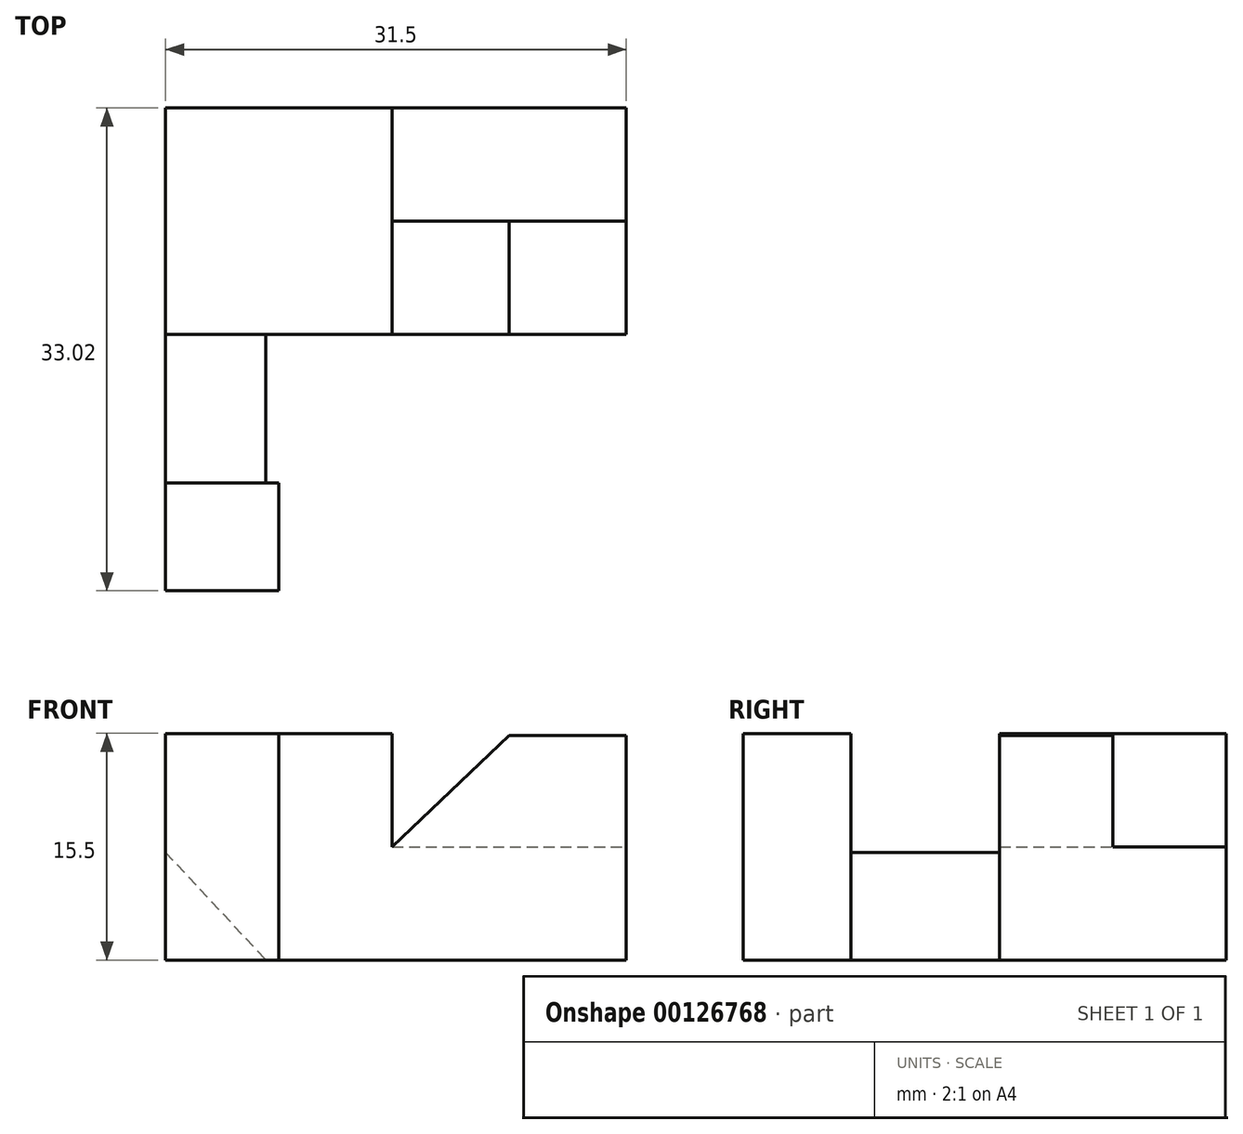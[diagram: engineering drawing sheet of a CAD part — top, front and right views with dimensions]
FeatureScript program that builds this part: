
annotation { "Feature Type Name" : "Feature", "Feature Type Description" : "" }
export const myFeature = defineFeature(function(context is Context, id is Id, definition is map)
    precondition{}
    {
        {
            var Q0;
            Q0=qCreatedBy(makeId("Front.planeOp"),FACE);
            var sketch = newSketch(context, id + "F0", { "sketchPlane" : qUnion([Q0])});
            skLineSegment(sketch, "E0.bottom", {"start": v(7.75, 7.75) * mm, "end": v(-7.75, 7.75) * mm});
            skLineSegment(sketch, "E0.top", {"start": v(7.75, -7.75) * mm, "end": v(-7.75, -7.75) * mm});
            skLineSegment(sketch, "E0.left", {"start": v(7.75, 7.75) * mm, "end": v(7.75, -7.75) * mm});
            skLineSegment(sketch, "E0.right", {"start": v(-7.75, 7.75) * mm, "end": v(-7.75, -7.75) * mm});
            skPoint(sketch, "E0.middle", {"position": v(0, 0) * mm});
            skSolve(sketch);
        }
        {
            var Q0;
            Q0=makeQuery(id+"F0.imprint","IMPRINT",FACE,{"disambiguationData":[TD([[makeQuery(id+"F0.imprint","IMPRINT",EDGE,{"derivedFrom":sQuery(id+"F0.wireOp",EDGE,"E0.bottom")}),1.0]])]});
            extrude(context, id + "F1", {"entities" : qUnion([Q0]), "endBound" : BoundingType.SYMMETRIC, "depth" : 15.5 * mm});
        }
        {
            var Q0;
            Q0=makeQuery(id+"F1.opExtrude","CAP_FACE",FACE,{"disambiguationData":[OSD([sQuery(id+"F0.wireOp",EDGE,"E0.bottom"),sQuery(id+"F0.wireOp",EDGE,"E0.top"),sQuery(id+"F0.wireOp",EDGE,"E0.left"),sQuery(id+"F0.wireOp",EDGE,"E0.right")])],"isStart":false});
            var sketch = newSketch(context, id + "F2", { "sketchPlane" : qUnion([Q0])});
            skLineSegment(sketch, "E1", {"start": v(-7.75, -7.75) * mm, "end": v(-7.75, -0.38) * mm});
            skLineSegment(sketch, "E2", {"start": v(-7.75, -7.75) * mm, "end": v(-0.89, -7.75) * mm});
            skLineSegment(sketch, "E3", {"start": v(-7.75, -0.38) * mm, "end": v(-0.89, -7.75) * mm});
            skSolve(sketch);
        }
        {
            var Q0;
            Q0=makeQuery(id+"F2.imprint","IMPRINT",FACE,{"disambiguationData":[TD([[makeQuery(id+"F2.imprint","IMPRINT",EDGE,{"derivedFrom":sQuery(id+"F2.wireOp",EDGE,"E1")}),1.0]])]});
            extrude(context, id + "F3", {"entities" : qUnion([Q0]), "operationType" : NewBodyOperationType.ADD, "depth" : 10.16 * mm});
        }
        {
            var Q0;
            Q0=makeQuery(id+"F3.opExtrude","CAP_FACE",FACE,{"disambiguationData":[OSD([sQuery(id+"F2.wireOp",EDGE,"E1"),sQuery(id+"F2.wireOp",EDGE,"E2"),sQuery(id+"F2.wireOp",EDGE,"E3")])],"isStart":false});
            var sketch = newSketch(context, id + "F4", { "sketchPlane" : qUnion([Q0])});
            skLineSegment(sketch, "E4.0", {"start": v(7.75, 7.75) * mm, "end": v(-7.75, 7.75) * mm});
            skLineSegment(sketch, "E5.0", {"start": v(7.75, -7.75) * mm, "end": v(-0.89, -7.75) * mm});
            skLineSegment(sketch, "E6", {"start": v(-7.75, 7.75) * mm, "end": v(-7.75, -7.75) * mm});
            skLineSegment(sketch, "E7", {"start": v(-7.75, -7.75) * mm, "end": v(0, -7.75) * mm});
            skLineSegment(sketch, "E8", {"start": v(0, -7.75) * mm, "end": v(0, 7.75) * mm});
            skSolve(sketch);
        }
        {
            var Q0;
            Q0 = qSketchRegion(id + "F4", true);
            extrude(context, id + "F5", {"entities" : qUnion([Q0]), "operationType" : NewBodyOperationType.ADD, "depth" : 7.37 * mm});
        }
        {
            var Q0;
            Q0=makeQuery(id+"F1.opExtrude","SWEPT_FACE",FACE,{"disambiguationData":[OSD([sQuery(id+"F0.wireOp",EDGE,"E0.left")])]});
            var sketch = newSketch(context, id + "F6", { "sketchPlane" : qUnion([Q0])});
            skLineSegment(sketch, "E9", {"start": v(-7.75, -7.75) * mm, "end": v(-7.75, 0) * mm});
            skLineSegment(sketch, "E10", {"start": v(-7.75, 0) * mm, "end": v(7.75, 0) * mm});
            skLineSegment(sketch, "E11", {"start": v(7.75, 0) * mm, "end": v(7.75, -7.75) * mm});
            skLineSegment(sketch, "E12", {"start": v(7.75, -7.75) * mm, "end": v(-7.75, -7.75) * mm});
            skSolve(sketch);
        }
        {
            var Q0;
            Q0=makeQuery(id+"F6.imprint","IMPRINT",FACE,{"disambiguationData":[TD([[makeQuery(id+"F6.imprint","IMPRINT",EDGE,{"derivedFrom":sQuery(id+"F6.wireOp",EDGE,"E9")}),1.0]])]});
            extrude(context, id + "F7", {"entities" : qUnion([Q0]), "operationType" : NewBodyOperationType.ADD, "depth" : 16 * mm});
        }
        {
            var Q0;
            Q0=makeQuery(id+"F7.opExtrude","SWEPT_FACE",FACE,{"disambiguationData":[OSD([sQuery(id+"F6.wireOp",EDGE,"E10")])]});
            var sketch = newSketch(context, id + "F8", { "sketchPlane" : qUnion([Q0])});
            skLineSegment(sketch, "E13", {"start": v(15.75, -7.75) * mm, "end": v(15.75, 0) * mm});
            skLineSegment(sketch, "E14", {"start": v(15.75, 0) * mm, "end": v(23.75, 0) * mm});
            skLineSegment(sketch, "E15", {"start": v(23.75, 0) * mm, "end": v(23.75, -7.75) * mm});
            skLineSegment(sketch, "E16", {"start": v(23.75, -7.75) * mm, "end": v(15.75, -7.75) * mm});
            skSolve(sketch);
        }
        {
            var Q0;
            Q0 = qSketchRegion(id + "F8", true);
            var Q1;
            Q1=makeQuery(id+"F8.imprint","IMPRINT",FACE,{"disambiguationData":[TD([[makeQuery(id+"F8.imprint","IMPRINT",EDGE,{"derivedFrom":sQuery(id+"F8.wireOp",EDGE,"E13")}),-1.0]])]});
            extrude(context, id + "F9", {"entities" : qUnion([Q0, Q1]), "operationType" : NewBodyOperationType.ADD, "depth" : 7.62 * mm});
        }
        {
            var Q0;
            Q0=makeQuery(id+"F9.boolean.opBoolean","MERGE",FACE,{"derivedFrom":[makeQuery(id+"F7.boolean.opBoolean","MERGE",FACE,{"derivedFrom":[makeQuery(id+"F1.opExtrude","CAP_FACE",FACE,{"disambiguationData":[OSD([sQuery(id+"F0.wireOp",EDGE,"E0.bottom"),sQuery(id+"F0.wireOp",EDGE,"E0.top"),sQuery(id+"F0.wireOp",EDGE,"E0.left"),sQuery(id+"F0.wireOp",EDGE,"E0.right")])],"isStart":false}),makeQuery(id+"F7.opExtrude","SWEPT_FACE",FACE,{"disambiguationData":[OSD([sQuery(id+"F6.wireOp",EDGE,"E9")])]})]}),makeQuery(id+"F9.opExtrude","SWEPT_FACE",FACE,{"disambiguationData":[OSD([sQuery(id+"F8.wireOp",EDGE,"E16")])]})]});
            var sketch = newSketch(context, id + "F10", { "sketchPlane" : qUnion([Q0])});
            skLineSegment(sketch, "E17", {"start": v(7.75, 0) * mm, "end": v(15.75, 7.62) * mm});
            skSolve(sketch);
        }
        {
            var Q0;
            Q0 = qSketchRegion(id + "F10", true);
            var Q1;
            Q1=makeQuery(id+"F10.imprint","IMPRINT",FACE,{"disambiguationData":[TD([[makeQuery(id+"F10.imprint","IMPRINT",EDGE,{"derivedFrom":sQuery(id+"F10.wireOp",EDGE,"E17")}),-1.0]])]});
            extrude(context, id + "F11", {"entities" : qUnion([Q0, Q1]), "operationType" : NewBodyOperationType.ADD, "oppositeDirection" : true, "depth" : 7.75 * mm});
        }
    });
